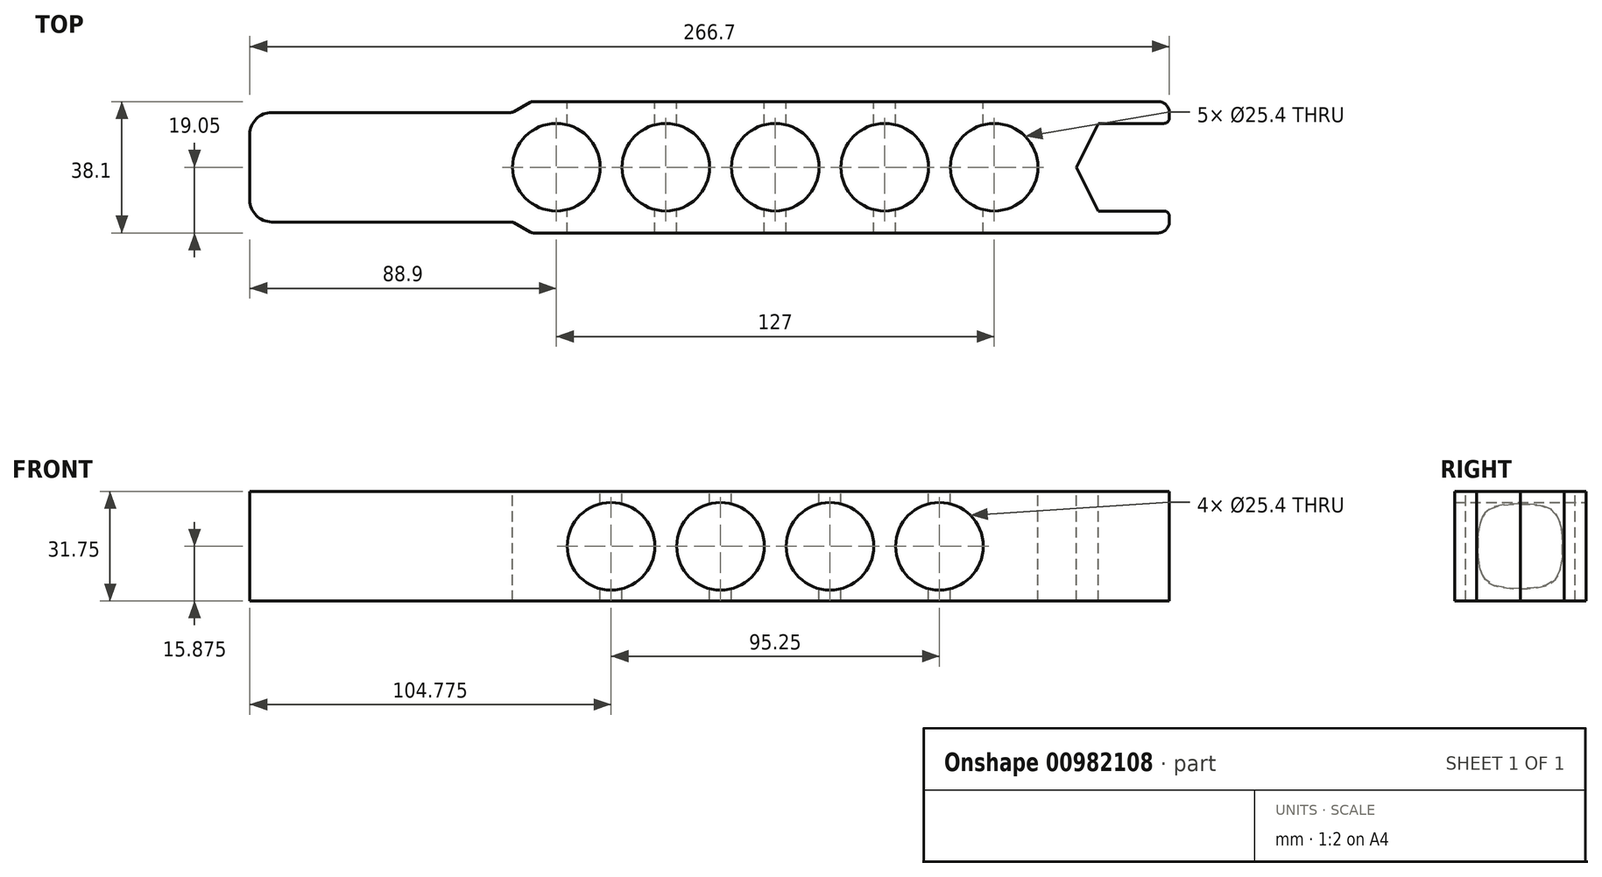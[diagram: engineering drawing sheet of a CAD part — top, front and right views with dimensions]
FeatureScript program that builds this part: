
annotation { "Feature Type Name" : "Feature", "Feature Type Description" : "" }
export const myFeature = defineFeature(function(context is Context, id is Id, definition is map)
    precondition{}
    {
        {
            var Q0;
            Q0=qCreatedBy(makeId("Top.planeOp"),FACE);
            var sketch = newSketch(context, id + "F0", { "sketchPlane" : qUnion([Q0])});
            skLineSegment(sketch, "E0.bottom", {"start": v(133.35, -19.05) * mm, "end": v(-133.35, -19.05) * mm});
            skLineSegment(sketch, "E0.top", {"start": v(133.35, 19.05) * mm, "end": v(-133.35, 19.05) * mm});
            skLineSegment(sketch, "E0.left", {"start": v(133.35, -19.05) * mm, "end": v(133.35, 19.05) * mm});
            skLineSegment(sketch, "E0.right", {"start": v(-133.35, -19.05) * mm, "end": v(-133.35, 19.05) * mm});
            skPoint(sketch, "E0.middle", {"position": v(0, 0) * mm});
            skLineSegment(sketch, "E1", {"start": v(133.35, 15.88) * mm, "end": v(133.35, 14.29) * mm});
            skLineSegment(sketch, "E2", {"start": v(131.76, 12.7) * mm, "end": v(112.71, 12.7) * mm});
            skLineSegment(sketch, "E3", {"start": v(133.35, -15.87) * mm, "end": v(133.35, -14.29) * mm});
            skLineSegment(sketch, "E4", {"start": v(131.76, -12.7) * mm, "end": v(112.71, -12.7) * mm});
            skLineSegment(sketch, "E5", {"start": v(106.36, 0) * mm, "end": v(112.71, 12.7) * mm});
            skLineSegment(sketch, "E6", {"start": v(112.71, -12.7) * mm, "end": v(106.36, 0) * mm});
            skLineSegment(sketch, "E7", {"start": v(-133.35, -19.05) * mm, "end": v(-133.35, -15.88) * mm});
            skLineSegment(sketch, "E8", {"start": v(-133.35, -9.53) * mm, "end": v(-133.35, 9.52) * mm});
            skLineSegment(sketch, "E9", {"start": v(-127, 15.87) * mm, "end": v(-57.58, 15.87) * mm});
            skLineSegment(sketch, "E10", {"start": v(-127, -15.88) * mm, "end": v(-57.58, -15.88) * mm});
            skLineSegment(sketch, "E11", {"start": v(-56.78, 16.09) * mm, "end": v(-52.02, 18.84) * mm});
            skLineSegment(sketch, "E12", {"start": v(-56.78, -16.09) * mm, "end": v(-52.02, -18.84) * mm});
            skLineSegment(sketch, "E13", {"start": v(-51.23, -19.05) * mm, "end": v(130.18, -19.05) * mm});
            skLineSegment(sketch, "E14", {"start": v(-51.23, 19.05) * mm, "end": v(130.18, 19.05) * mm});
            skPoint(sketch, "E15.visualSharp", {"position": v(133.35, 19.05) * mm});
            skArc(sketch, "E15.filletArc", {"start": v(133.35, 15.88) * mm, "mid": v(132.42, 18.12) * mm, "end": v(130.18, 19.05) * mm});
            skPoint(sketch, "E16.visualSharp", {"position": v(133.35, 12.7) * mm});
            skArc(sketch, "E16.filletArc", {"start": v(131.76, 12.7) * mm, "mid": v(132.89, 13.16) * mm, "end": v(133.35, 14.29) * mm});
            skPoint(sketch, "E17.visualSharp", {"position": v(133.35, -12.7) * mm});
            skArc(sketch, "E17.filletArc", {"start": v(133.35, -14.29) * mm, "mid": v(132.89, -13.16) * mm, "end": v(131.76, -12.7) * mm});
            skPoint(sketch, "E18.visualSharp", {"position": v(133.35, -19.05) * mm});
            skArc(sketch, "E18.filletArc", {"start": v(130.18, -19.05) * mm, "mid": v(132.42, -18.12) * mm, "end": v(133.35, -15.87) * mm});
            skPoint(sketch, "E19.visualSharp", {"position": v(-133.35, 15.87) * mm});
            skArc(sketch, "E19.filletArc", {"start": v(-127, 15.87) * mm, "mid": v(-131.5, 14.02) * mm, "end": v(-133.35, 9.52) * mm});
            skPoint(sketch, "E20.visualSharp", {"position": v(-133.35, -15.88) * mm});
            skArc(sketch, "E20.filletArc", {"start": v(-133.35, -9.53) * mm, "mid": v(-131.5, -14.02) * mm, "end": v(-127, -15.88) * mm});
            skPoint(sketch, "E21.visualSharp", {"position": v(-57.15, 15.87) * mm});
            skArc(sketch, "E21.filletArc", {"start": v(-57.58, 15.88) * mm, "mid": v(-57.16, 15.93) * mm, "end": v(-56.78, 16.09) * mm});
            skPoint(sketch, "E22.visualSharp", {"position": v(-51.65, 19.05) * mm});
            skArc(sketch, "E22.filletArc", {"start": v(-51.23, 19.05) * mm, "mid": v(-51.64, 19) * mm, "end": v(-52.02, 18.84) * mm});
            skPoint(sketch, "E23.visualSharp", {"position": v(-57.15, -15.88) * mm});
            skArc(sketch, "E23.filletArc", {"start": v(-56.78, -16.09) * mm, "mid": v(-57.16, -15.93) * mm, "end": v(-57.58, -15.87) * mm});
            skPoint(sketch, "E24.visualSharp", {"position": v(-51.65, -19.05) * mm});
            skArc(sketch, "E24.filletArc", {"start": v(-52.02, -18.84) * mm, "mid": v(-51.64, -19) * mm, "end": v(-51.23, -19.05) * mm});
            skSolve(sketch);
        }
        {
            var Q0;
            Q0=makeQuery(id+"F0.imprint","IMPRINT",FACE,{"disambiguationData":[TD([[makeQuery(id+"F0.imprint","IMPRINT",EDGE,{"derivedFrom":sQuery(id+"F0.wireOp",EDGE,"E2")}),-1.0]])]});
            extrude(context, id + "F1", {"entities" : qUnion([Q0]), "oppositeDirection" : true, "depth" : 31.75 * mm, "offsetDistance" : 25.4 * mm});
        }
        {
            var Q0;
            Q0=qCreatedBy(makeId("Top.planeOp"),FACE);
            var sketch = newSketch(context, id + "F2", { "sketchPlane" : qUnion([Q0])});
            skLineSegment(sketch, "E25", {"start": v(-133.35, 0) * mm, "end": v(-57.15, 0) * mm});
            skLineSegment(sketch, "E26", {"start": v(-57.15, 0) * mm, "end": v(-57.15, 19.05) * mm});
            skLineSegment(sketch, "E27", {"start": v(-57.15, 0) * mm, "end": v(-44.45, 0) * mm});
            skCircle(sketch, "E28", {"center": v(-44.45, 0) * mm, "radius": 12.7 * mm});
            skCircle(sketch, "E29.1.0.0", {"center": v(-12.7, 0) * mm, "radius": 12.7 * mm});
            skCircle(sketch, "E29.2.0.0", {"center": v(19.05, 0) * mm, "radius": 12.7 * mm});
            skCircle(sketch, "E29.3.0.0", {"center": v(50.8, 0) * mm, "radius": 12.7 * mm});
            skCircle(sketch, "E29.4.0.0", {"center": v(82.55, 0) * mm, "radius": 12.7 * mm});
            skLineSegment(sketch, "E29.direction1", {"start": v(-44.45, 0) * mm, "end": v(-12.7, 0) * mm, "construction": true});
            skSolve(sketch);
        }
        {
            var Q0;
            Q0=sQuery(id+"F2.wireOp",VERTEX,"E27.end");
            var Q1;
            Q1=sQuery(id+"F2.wireOp",VERTEX,"E29.direction1.end");
            var Q2;
            Q2=sQuery(id+"F2.wireOp",VERTEX,"E29.2.0.0.center");
            var Q3;
            Q3=sQuery(id+"F2.wireOp",VERTEX,"E29.3.0.0.center");
            var Q4;
            Q4=sQuery(id+"F2.wireOp",VERTEX,"E29.4.0.0.center");
            var Q5;
            Q5=makeQuery(id+"F1.opExtrude","SWEPT_BODY",BODY,{"disambiguationData":[OSD([sQuery(id+"F0.wireOp",EDGE,"E0.bottom"),sQuery(id+"F0.wireOp",EDGE,"E0.top"),sQuery(id+"F0.wireOp",EDGE,"E0.left"),sQuery(id+"F0.wireOp",EDGE,"E0.right"),sQuery(id+"F0.wireOp",EDGE,"E2"),sQuery(id+"F0.wireOp",EDGE,"E4"),sQuery(id+"F0.wireOp",EDGE,"E5"),sQuery(id+"F0.wireOp",EDGE,"E6"),sQuery(id+"F0.wireOp",EDGE,"E9"),sQuery(id+"F0.wireOp",EDGE,"E10"),sQuery(id+"F0.wireOp",EDGE,"E11"),sQuery(id+"F0.wireOp",EDGE,"E12"),sQuery(id+"F0.wireOp",EDGE,"E15.filletArc"),sQuery(id+"F0.wireOp",EDGE,"E16.filletArc"),sQuery(id+"F0.wireOp",EDGE,"E17.filletArc"),sQuery(id+"F0.wireOp",EDGE,"E18.filletArc"),sQuery(id+"F0.wireOp",EDGE,"E19.filletArc"),sQuery(id+"F0.wireOp",EDGE,"E20.filletArc"),sQuery(id+"F0.wireOp",EDGE,"E21.filletArc"),sQuery(id+"F0.wireOp",EDGE,"E22.filletArc"),sQuery(id+"F0.wireOp",EDGE,"E23.filletArc"),sQuery(id+"F0.wireOp",EDGE,"E24.filletArc")])]});
            hole(context, id + "F3", {"style" : HoleStyle.SIMPLE, "endStyle" : HoleEndStyle.THROUGH, "holeDiameter" : 25.4 * mm, "majorDiameter" : 6.35 * mm, "isTappedThrough" : true, "tappedDepth" : 12.7 * mm, "tapClearance" : 3, "locations" : qUnion([Q0, Q1, Q2, Q3, Q4]), "scope" : qUnion([Q5])});
        }
        {
            var Q0;
            Q0=makeQuery(id+"F1.opExtrude","SWEPT_FACE",FACE,{"disambiguationData":[OSD([sQuery(id+"F0.wireOp",EDGE,"E0.top")])]});
            var Q1;
            Q1=makeQuery(id+"F1.opExtrude","SWEPT_FACE",FACE,{"disambiguationData":[OSD([sQuery(id+"F0.wireOp",EDGE,"E0.top")])]});
            var sketch = newSketch(context, id + "F4", { "sketchPlane" : qUnion([Q0, Q1])});
            skLineSegment(sketch, "E30", {"start": v(127, -15.88) * mm, "end": v(44.45, -15.88) * mm});
            skLineSegment(sketch, "E31", {"start": v(44.45, -15.88) * mm, "end": v(28.58, -15.88) * mm});
            skPoint(sketch, "E32", {"position": v(28.58, -15.88) * mm});
            skPoint(sketch, "E33.1.0.0", {"position": v(-3.17, -15.88) * mm});
            skPoint(sketch, "E33.2.0.0", {"position": v(-34.92, -15.88) * mm});
            skPoint(sketch, "E33.3.0.0", {"position": v(-66.67, -15.88) * mm});
            skLineSegment(sketch, "E33.direction1", {"start": v(28.58, -15.88) * mm, "end": v(-3.17, -15.88) * mm, "construction": true});
            skPoint(sketch, "E34.0.4.0", {"position": v(-98.42, -15.88) * mm});
            skSolve(sketch);
        }
        {
            var Q0;
            Q0=sQuery(id+"F4.wireOp",VERTEX,"E32");
            var Q1;
            Q1=sQuery(id+"F4.wireOp",VERTEX,"E33.1.0.0");
            var Q2;
            Q2=sQuery(id+"F4.wireOp",VERTEX,"E33.2.0.0");
            var Q3;
            Q3=sQuery(id+"F4.wireOp",VERTEX,"E33.3.0.0");
            var Q4;
            Q4=makeQuery(id+"F1.opExtrude","SWEPT_BODY",BODY,{"disambiguationData":[OSD([sQuery(id+"F0.wireOp",EDGE,"E0.bottom"),sQuery(id+"F0.wireOp",EDGE,"E0.top"),sQuery(id+"F0.wireOp",EDGE,"E0.left"),sQuery(id+"F0.wireOp",EDGE,"E0.right"),sQuery(id+"F0.wireOp",EDGE,"E2"),sQuery(id+"F0.wireOp",EDGE,"E4"),sQuery(id+"F0.wireOp",EDGE,"E5"),sQuery(id+"F0.wireOp",EDGE,"E6"),sQuery(id+"F0.wireOp",EDGE,"E9"),sQuery(id+"F0.wireOp",EDGE,"E10"),sQuery(id+"F0.wireOp",EDGE,"E11"),sQuery(id+"F0.wireOp",EDGE,"E12"),sQuery(id+"F0.wireOp",EDGE,"E15.filletArc"),sQuery(id+"F0.wireOp",EDGE,"E16.filletArc"),sQuery(id+"F0.wireOp",EDGE,"E17.filletArc"),sQuery(id+"F0.wireOp",EDGE,"E18.filletArc"),sQuery(id+"F0.wireOp",EDGE,"E19.filletArc"),sQuery(id+"F0.wireOp",EDGE,"E20.filletArc"),sQuery(id+"F0.wireOp",EDGE,"E21.filletArc"),sQuery(id+"F0.wireOp",EDGE,"E22.filletArc"),sQuery(id+"F0.wireOp",EDGE,"E23.filletArc"),sQuery(id+"F0.wireOp",EDGE,"E24.filletArc")])]});
            hole(context, id + "F5", {"style" : HoleStyle.SIMPLE, "endStyle" : HoleEndStyle.THROUGH, "holeDiameter" : 25.4 * mm, "majorDiameter" : 6.35 * mm, "isTappedThrough" : true, "tappedDepth" : 12.7 * mm, "tapClearance" : 3, "locations" : qUnion([Q0, Q1, Q2, Q3]), "scope" : qUnion([Q4])});
        }
    });
